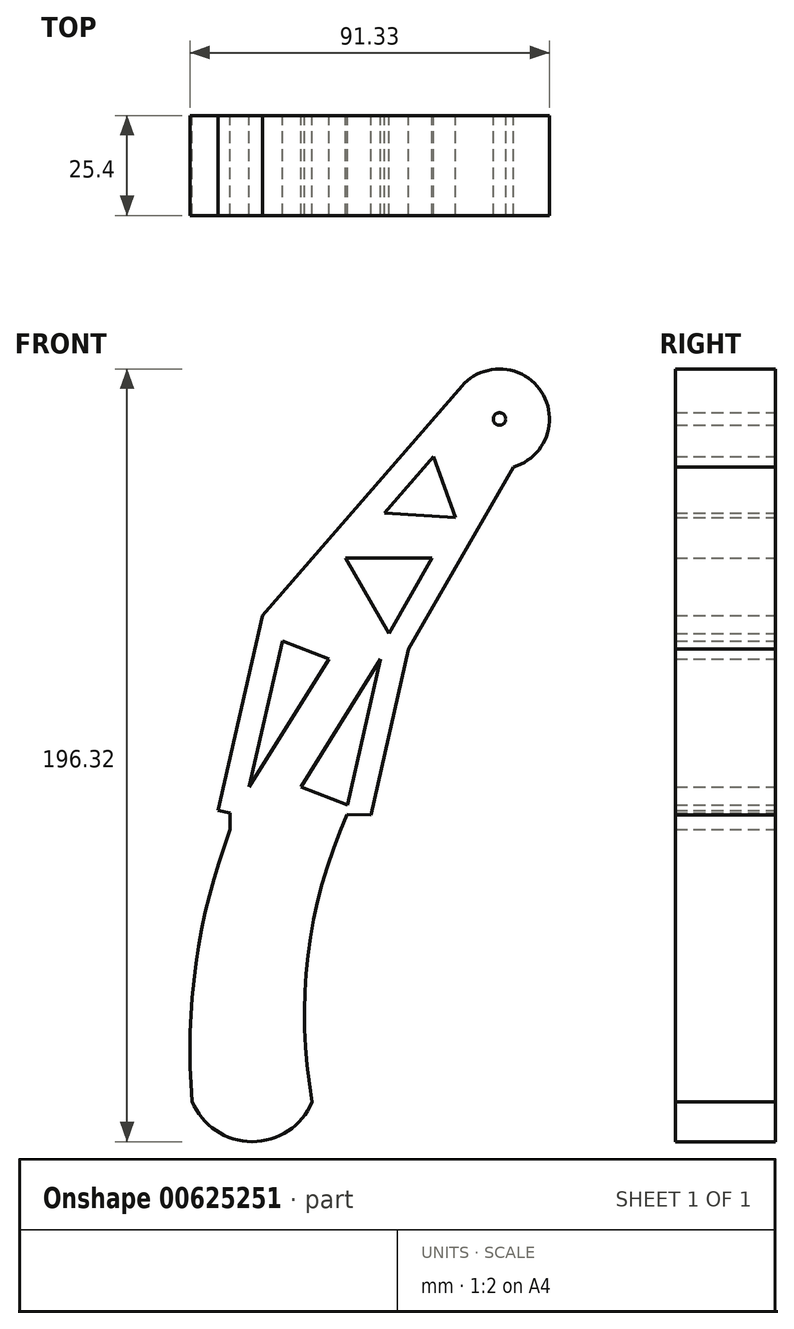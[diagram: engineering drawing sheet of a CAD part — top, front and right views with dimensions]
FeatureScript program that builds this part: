
annotation { "Feature Type Name" : "Feature", "Feature Type Description" : "" }
export const myFeature = defineFeature(function(context is Context, id is Id, definition is map)
    precondition{}
    {
        {
            var Q0;
            Q0=qCreatedBy(makeId("Front.planeOp"),FACE);
            var sketch = newSketch(context, id + "F0", { "sketchPlane" : qUnion([Q0])});
            skArc(sketch, "E0", {"start": v(-39.97, 101.64) * mm, "mid": v(-32.85, 120.68) * mm, "end": v(-53.13, 122.16) * mm});
            skCircle(sketch, "E1", {"center": v(-43.54, 113.83) * mm, "radius": 1.59 * mm});
            skLineSegment(sketch, "E2", {"start": v(-53.13, 122.16) * mm, "end": v(-103.76, 63.95) * mm});
            skLineSegment(sketch, "E3", {"start": v(-103.76, 63.95) * mm, "end": v(-115.05, 14.42) * mm});
            skLineSegment(sketch, "E4", {"start": v(-39.97, 101.64) * mm, "end": v(-66.64, 55.33) * mm});
            skPoint(sketch, "E4.endSnap0", {"position": v(-66.64, 121.35) * mm});
            skLineSegment(sketch, "E5", {"start": v(-66.64, 55.33) * mm, "end": v(-76.25, 13.23) * mm});
            skArc(sketch, "E6", {"start": v(-111.95, 9.48) * mm, "mid": v(-120.65, -24.5) * mm, "end": v(-121.6, -59.57) * mm});
            skLineSegment(sketch, "E7", {"start": v(-115.05, 14.42) * mm, "end": v(-111.95, 13.71) * mm});
            skLineSegment(sketch, "E8", {"start": v(-111.95, 13.71) * mm, "end": v(-111.95, 9.48) * mm});
            skLineSegment(sketch, "E9", {"start": v(-76.25, 13.23) * mm, "end": v(-82.27, 13.32) * mm});
            skArc(sketch, "E10", {"start": v(-82.27, 13.32) * mm, "mid": v(-92.19, -22.53) * mm, "end": v(-91.12, -59.72) * mm});
            skArc(sketch, "E11", {"start": v(-121.6, -59.57) * mm, "mid": v(-106.41, -69.79) * mm, "end": v(-91.12, -59.72) * mm});
            skLineSegment(sketch, "E12", {"start": v(-60.3, 104.24) * mm, "end": v(-72.8, 89.87) * mm});
            skLineSegment(sketch, "E13", {"start": v(-60.3, 104.24) * mm, "end": v(-54.74, 88.72) * mm});
            skLineSegment(sketch, "E14", {"start": v(-72.8, 89.87) * mm, "end": v(-54.74, 88.72) * mm});
            skLineSegment(sketch, "E15", {"start": v(-60.63, 78.48) * mm, "end": v(-71.66, 59.35) * mm});
            skPoint(sketch, "E15.startSnap0", {"position": v(-53.3, 78.48) * mm});
            skLineSegment(sketch, "E16", {"start": v(-71.66, 59.35) * mm, "end": v(-82.72, 78.46) * mm});
            skLineSegment(sketch, "E17", {"start": v(-82.72, 78.46) * mm, "end": v(-60.63, 78.48) * mm});
            skLineSegment(sketch, "E18", {"start": v(-98.72, 57.46) * mm, "end": v(-107.2, 20.3) * mm});
            skLineSegment(sketch, "E19", {"start": v(-107.2, 20.3) * mm, "end": v(-86.89, 52.85) * mm});
            skLineSegment(sketch, "E20", {"start": v(-86.89, 52.85) * mm, "end": v(-98.72, 57.46) * mm});
            skLineSegment(sketch, "E21", {"start": v(-73.72, 52.85) * mm, "end": v(-94.03, 20.3) * mm});
            skLineSegment(sketch, "E22", {"start": v(-94.03, 20.3) * mm, "end": v(-82.2, 15.7) * mm});
            skLineSegment(sketch, "E23", {"start": v(-82.2, 15.7) * mm, "end": v(-73.72, 52.85) * mm});
            skSolve(sketch);
        }
        {
            var Q0;
            Q0 = qSketchRegion(id + "F0", true);
            extrude(context, id + "F1", {"entities" : qUnion([Q0]), "depth" : 25.4 * mm, "offsetDistance" : 25.4 * mm});
        }
    });
